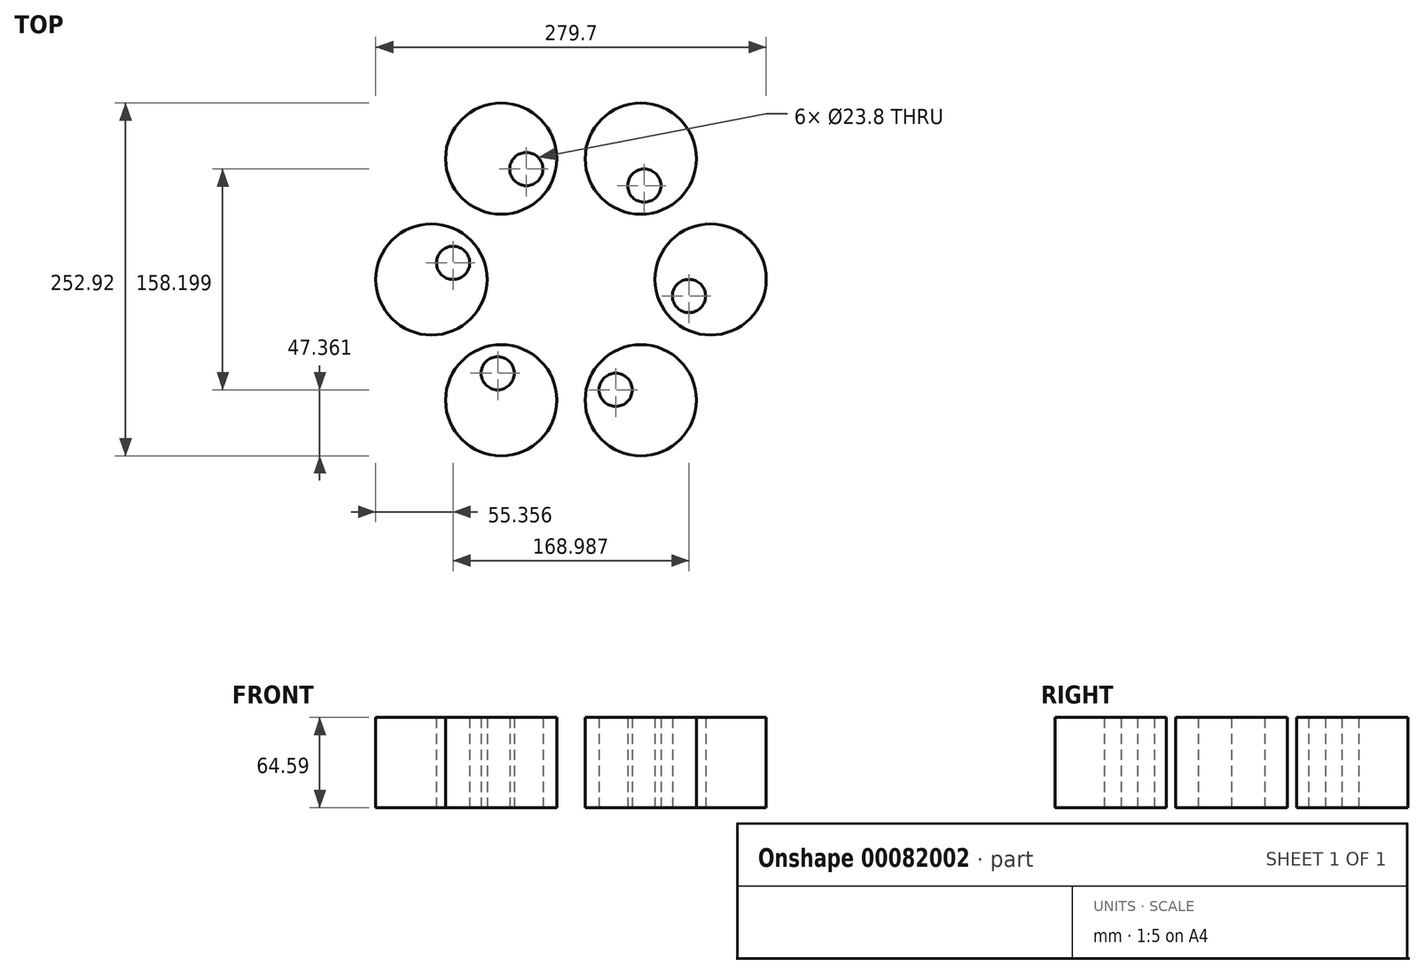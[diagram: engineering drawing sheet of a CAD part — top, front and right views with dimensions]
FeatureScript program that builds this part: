
annotation { "Feature Type Name" : "Feature", "Feature Type Description" : "" }
export const myFeature = defineFeature(function(context is Context, id is Id, definition is map)
    precondition{}
    {
        {
            var Q0;
            Q0=qCreatedBy(makeId("Top.planeOp"),FACE);
            var sketch = newSketch(context, id + "F0", { "sketchPlane" : qUnion([Q0])});
            skCircle(sketch, "E0", {"center": v(0, 0) * mm, "radius": 39.85 * mm});
            skCircle(sketch, "E1", {"center": v(15.5, 11.85) * mm, "radius": 11.9 * mm});
            skSolve(sketch);
        }
        {
            var Q0;
            Q0=makeQuery(id+"F0.imprint","IMPRINT",FACE,{"disambiguationData":[TD([[makeQuery(id+"F0.imprint","IMPRINT",EDGE,{"derivedFrom":sQuery(id+"F0.wireOp",EDGE,"E0")}),1.0]])]});
            extrude(context, id + "F1", {"entities" : qUnion([Q0]), "depth" : 64.6 * mm});
        }
        {
            var Q0;
            Q0=qCreatedBy(makeId("Front.planeOp"),FACE);
            var sketch = newSketch(context, id + "F2", { "sketchPlane" : qUnion([Q0])});
            skLineSegment(sketch, "E2", {"start": v(100, 0) * mm, "end": v(100, 75) * mm});
            skSolve(sketch);
        }
        {
            var Q0;
            Q0=makeQuery(id+"F1.opExtrude","SWEPT_BODY",BODY,{"disambiguationData":[OSD([sQuery(id+"F0.wireOp",EDGE,"E0"),sQuery(id+"F0.wireOp",EDGE,"E1")])]});
            var Q1;
            Q1=sQuery(id+"F2.wireOp",EDGE,"E2");
            circularPattern(context, id + "F3", {"entities" : qUnion([Q0]), "axis" : qUnion([Q1]), "angle" : 60 * degree, "instanceCount" : 6, "oppositeDirection" : true});
        }
    });
